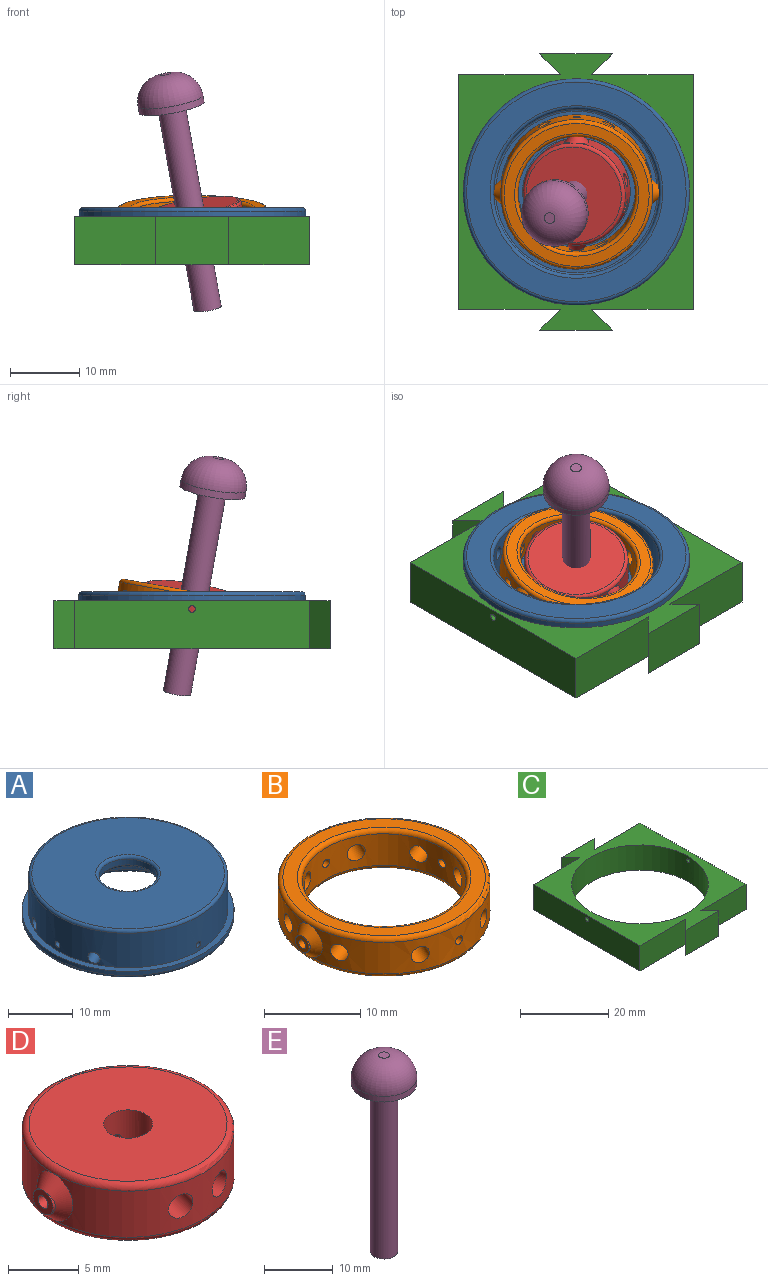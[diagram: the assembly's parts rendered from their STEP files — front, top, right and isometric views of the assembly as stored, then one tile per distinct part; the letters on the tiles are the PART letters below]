
ASSEMBLY  parts=5 mates=4
PART A: 26 faces, bbox 35.5x35.5x8.3 mm
  f0: cylinder r=12mm len=24mm, axis (0,0,-1), area 435.9mm2, adj f6,f7,f8,f9,f10,f11,f12,f13
  f1: cylinder r=15.4mm len=30.8mm, axis (0,0,-1), area 613.2mm2, adj f5,f6,f7,f8,f9,f10,f11,f12
  f2: plane 29.8x29.8mm, normal (0,0,1), area 618.9mm2, adj f18,f22
  f3: plane 31.8x31.8mm, normal (0,0,-1), area 303.4mm2, adj f20,f21
  f4: cylinder r=16.4mm len=32.8mm, axis (0,0,-1), area 81.4mm2, adj f5,f20
  f5: plane 32.8x32.8mm, normal (0,0,1), area 99.9mm2, adj f1,f4
  f6: cylinder r=0.5mm len=3.4mm, axis (0,1,0), area 10.7mm2, adj f0,f1
  f7: cylinder r=0.5mm len=3.4mm, axis (0,1,0), area 10.7mm2, adj f0,f1
  f8: cylinder r=1mm len=3.94mm, axis (-0.91,0.42,0), area 21.4mm2, adj f0,f1
  f9: cylinder r=1mm len=3.94mm, axis (-0.91,0.42,0), area 21.4mm2, adj f0,f1
  f10: cylinder r=1mm len=3.94mm, axis (-0.91,-0.42,0), area 21.4mm2, adj f0,f1
  f11: cylinder r=1mm len=3.94mm, axis (-0.91,-0.42,0), area 21.4mm2, adj f0,f1
  f12: cylinder r=0.5mm len=3.4mm, axis (1,0,0), area 10.7mm2, adj f0,f1
  f13: cylinder r=0.5mm len=3.4mm, axis (1,0,0), area 10.7mm2, adj f0,f1
  f14: plane 23.4x23.4mm, normal (0,0,-1), area 238.9mm2, adj f23,f25
  f15: cylinder r=7.5mm len=15mm, axis (0,0,1), area 0.5mm2, adj f23,f24
  f16: cylinder r=4.5mm len=9mm, axis (0,0,1), area 31.4mm2, adj f18,f19
  f17: plane 14.4x14.4mm, normal (0,0,-1), area 84.3mm2, adj f19,f24
  f18: torus R=5mm, axis (0,0,1), area 23.1mm2, adj f2,f16
  f19: torus R=5mm, axis (0,0,1), area 23.1mm2, adj f16,f17
  f20: torus R=15.9mm, axis (0,0,1), area 80mm2, adj f3,f4
  f21: torus R=12.5mm, axis (0,0,1), area 60.1mm2, adj f0,f3
  f22: torus R=14.9mm, axis (0,0,1), area 75.1mm2, adj f1,f2
  f23: torus R=7.8mm, axis (0,0,1), area 22.5mm2, adj f14,f15
  f24: torus R=7.2mm, axis (0,0,1), area 21.9mm2, adj f15,f17
  f25: torus R=11.7mm, axis (0,0,1), area 35.2mm2, adj f0,f14
PART B: 29 faces, bbox 24x23.8x5 mm
  f0: cylinder r=1mm len=2mm, axis (-1,0,0), area 0mm2, adj f10,f28
  f1: cylinder r=11mm len=22mm, axis (0,0,-1), area 113.3mm2, adj f13,f15,f17,f20,f21,f24,f26,f27
  f2: cylinder r=1mm len=2mm, axis (-1,0,0), area 0mm2, adj f8,f27
  f3: cylinder r=11mm len=22mm, axis (0,0,-1), area 113.3mm2, adj f14,f16,f18,f19,f22,f24,f26,f27
  f4: cylinder r=8.5mm len=17mm, axis (0,0,-1), area 185.3mm2, adj f11,f12,f13,f14,f15,f16,f17,f18
  f5: plane 21x21mm, normal (0,0,1), area 91.9mm2, adj f25,f26
  f6: plane 21x21mm, normal (0,0,-1), area 91.9mm2, adj f23,f24
  f7: cylinder r=1mm len=2mm, axis (-1,0,0), area 0mm2, adj f8,f27
  f8: plane 2x2mm, normal (1,0,0), area 2.4mm2, adj f2,f7,f12
  f9: cylinder r=1mm len=2mm, axis (-1,0,0), area 0mm2, adj f10,f28
  f10: plane 2x2mm, normal (-1,0,0), area 2.4mm2, adj f0,f9,f11
  f11: cylinder r=0.5mm len=3.5mm, axis (1,0,0), area 11mm2, adj f4,f10
  f12: cylinder r=0.5mm len=3.5mm, axis (1,0,0), area 11mm2, adj f4,f8
  f13: cylinder r=1mm len=3.12mm, axis (0.42,0.91,0), area 15.8mm2, adj f1,f4
  f14: cylinder r=1mm len=3.12mm, axis (0.42,0.91,0), area 15.8mm2, adj f3,f4
  f15: cylinder r=1mm len=3.12mm, axis (-0.42,0.91,0), area 15.8mm2, adj f1,f4
  f16: cylinder r=1mm len=3.12mm, axis (-0.42,0.91,0), area 15.8mm2, adj f3,f4
  f17: cylinder r=1mm len=3.05mm, axis (0.94,0.34,0), area 15.8mm2, adj f1,f4
  f18: cylinder r=1mm len=3.05mm, axis (0.94,0.34,0), area 15.8mm2, adj f3,f4
  f19: cylinder r=1mm len=3.05mm, axis (0.94,-0.34,0), area 15.8mm2, adj f3,f4
  f20: cylinder r=1mm len=3.05mm, axis (0.94,-0.34,0), area 15.8mm2, adj f1,f4
  f21: cylinder r=0.5mm len=2.5mm, axis (0,1,0), area 7.9mm2, adj f1,f4
  f22: cylinder r=0.5mm len=2.5mm, axis (0,1,0), area 7.9mm2, adj f3,f4
  f23: torus R=9mm, axis (0,0,1), area 42.8mm2, adj f4,f6
  f24: torus R=10.5mm, axis (0,0,1), area 53.4mm2, adj f1,f3,f6
  f25: torus R=9mm, axis (0,0,1), area 42.8mm2, adj f4,f5
  f26: torus R=10.5mm, axis (0,0,1), area 53.4mm2, adj f1,f3,f5
  f27: bspline ~4x3.67mm, area 12.4mm2, adj f1,f2,f3,f7
  f28: bspline ~4x3.67mm, area 12.4mm2, adj f0,f1,f3,f9
PART C: 17 faces, bbox 34x40x7 mm
  f0: plane 14.75x7mm, normal (0,1,0), area 103.3mm2, adj f3,f7,f8,f14
  f1: plane 14.75x7mm, normal (0,-1,0), area 103.3mm2, adj f3,f7,f8,f9
  f2: plane 14.75x7mm, normal (0,-1,0), area 103.3mm2, adj f5,f7,f8,f10
  f3: plane 34x7mm, normal (1,0,0), area 237.2mm2, adj f0,f1,f7,f8,f15
  f4: plane 14.75x7mm, normal (0,1,0), area 103.3mm2, adj f5,f7,f8,f13
  f5: plane 34x7mm, normal (-1,0,0), area 237.2mm2, adj f2,f4,f7,f8,f16
  f6: cylinder r=15.5mm len=31mm, axis (0,0,-1), area 680.2mm2, adj f7,f8,f15,f16
  f7: plane 40x34mm, normal (0,0,1), area 446.2mm2, adj f0,f1,f2,f3,f4,f5,f6,f9
  f8: plane 40x34mm, normal (0,0,-1), area 446.2mm2, adj f0,f1,f2,f3,f4,f5,f6,f9
  f9: plane 7x3mm, normal (0.71,0.71,0), area 29.7mm2, adj f1,f7,f8,f11
  f10: plane 7x3mm, normal (-0.71,0.71,0), area 29.7mm2, adj f2,f7,f8,f11
  f11: plane 10.5x7mm, normal (0,-1,0), area 73.5mm2, adj f7,f8,f9,f10
  f12: plane 10.5x7mm, normal (0,1,0), area 73.5mm2, adj f7,f8,f13,f14
  f13: plane 7x3mm, normal (-0.71,-0.71,0), area 29.7mm2, adj f4,f7,f8,f12
  f14: plane 7x3mm, normal (0.71,-0.71,0), area 29.7mm2, adj f0,f7,f8,f12
  f15: cylinder r=0.5mm len=1.51mm, axis (1,0,0), area 4.7mm2, adj f3,f6
  f16: cylinder r=0.5mm len=1.5mm, axis (1,0,0), area 4.7mm2, adj f5,f6
PART D: 29 faces, bbox 17x16.2x5 mm
  f0: cylinder r=1mm len=2mm, axis (-1,0,0), area 0mm2, adj f1,f28
  f1: plane 2x2mm, normal (-1,0,0), area 2.4mm2, adj f0,f2,f3
  f2: cylinder r=1mm len=2mm, axis (-1,0,0), area 0mm2, adj f1,f28
  f3: cylinder r=0.5mm len=6.77mm, axis (1,0,0), area 21.3mm2, adj f1,f4
  f4: cylinder r=1.73mm len=5mm, axis (0,0,-1), area 50.2mm2, adj f3,f5,f22,f23,f24,f25,f26,f27
  f5: cylinder r=0.5mm len=2.51mm, axis (-0.26,0.97,0), area 7.3mm2, adj f4,f6,f22
  f6: plane 2x1.93mm, normal (0.26,-0.97,0), area 2.4mm2, adj f5,f7
  f7: cylinder r=1mm len=3.83mm, axis (0.26,-0.97,0), area 21.6mm2, adj f6,f8
  f8: cylinder r=7.5mm len=15mm, axis (0,0,-1), area 76.8mm2, adj f7,f9,f11,f17,f21,f28
  f9: cylinder r=1mm len=3.83mm, axis (-0.26,-0.97,0), area 21.6mm2, adj f8,f10
  f10: plane 2x1.93mm, normal (-0.26,-0.97,0), area 2.4mm2, adj f9,f22
  f11: torus R=7mm, axis (0,0,1), area 36.1mm2, adj f8,f12,f26
  f12: cylinder r=7.5mm len=15mm, axis (0,0,-1), area 76.8mm2, adj f11,f13,f15,f17,f21,f28
  f13: cylinder r=1mm len=3.83mm, axis (0.26,0.97,0), area 21.6mm2, adj f12,f14
  f14: plane 2x1.93mm, normal (0.26,0.97,0), area 2.4mm2, adj f13,f24
  f15: cylinder r=1mm len=3.83mm, axis (-0.26,0.97,0), area 21.6mm2, adj f12,f16
  f16: plane 2x1.93mm, normal (-0.26,0.97,0), area 2.4mm2, adj f15,f23
  f17: bspline ~4x3.53mm, area 12.1mm2, adj f8,f12,f18,f20
  f18: cylinder r=1mm len=2mm, axis (-1,0,0), area 0mm2, adj f17,f19
  f19: plane 2x2mm, normal (1,0,0), area 2.4mm2, adj f18,f20,f27
  f20: cylinder r=1mm len=2mm, axis (-1,0,0), area 0mm2, adj f17,f19
  f21: torus R=7mm, axis (0,0,1), area 36.1mm2, adj f8,f12,f25
  f22: cylinder r=0.5mm len=2.51mm, axis (-0.26,-0.97,0), area 7.3mm2, adj f4,f5,f10
  f23: cylinder r=0.5mm len=2.52mm, axis (-0.26,0.97,0), area 7.3mm2, adj f4,f16,f24
  f24: cylinder r=0.5mm len=2.51mm, axis (-0.26,-0.97,0), area 7.3mm2, adj f4,f14,f23
  f25: plane 14x14mm, normal (0,0,-1), area 144.5mm2, adj f4,f21
  f26: plane 14x14mm, normal (0,0,1), area 144.5mm2, adj f4,f11
  f27: cylinder r=0.5mm len=6.77mm, axis (1,0,0), area 21.3mm2, adj f4,f19
  f28: bspline ~4x3.53mm, area 12.1mm2, adj f0,f2,f8,f12
PART E: 6 faces, bbox 9.6x9.6x35 mm
  f0: cylinder r=2mm len=30mm, axis (0,0,-1), area 377mm2, adj f1,f4
  f1: plane 4x4mm, normal (0,0,-1), area 12.6mm2, adj f0
  f2: cylinder r=4.78mm len=9.56mm, axis (0,0,-1), area 30mm2, adj f4,f5
  f3: plane 1.56x1.56mm, normal (0,0,1), area 1.9mm2, adj f5
  f4: plane 9.56x9.56mm, normal (0,0,-1), area 59.3mm2, adj f0,f2
  f5: torus R=0.78mm, axis (0,0,1), area 131.4mm2, adj f2,f3
PLACE A rot(axis=(-0.71,-0.71,0),180deg) t=(0.08,0.01,4.78)mm
PLACE B rot(axis=(1,0,0),10deg) t=(0.12,0.44,-0.18)mm
PLACE C t=(0.02,0.01,-3.51)mm fixed
PLACE D rot(axis=(0.17,0,-0.99),91.7deg) t=(0.55,0.47,-0.14)mm
PLACE E rot(axis=(0.71,-0.71,-0.06),14.1deg) t=(2.29,2.18,-9.83)mm
MATE revolute D.f0 <-> B.f21  axis (0,-0.98,-0.17) through (0.12,-8.33,0.81)mm
MATE revolute B.f0 <-> A.f6  axis (1,0,0) through (-11.88,0.01,2.28)mm
MATE fastened C.f15 <-> A.f6  axis (1,0,0) through (15.5,0.01,2.28)mm
MATE slider E.f0 <-> D.f4  axis (0.17,0.17,-0.97) through (-0.32,-0.39,4.71)mm
